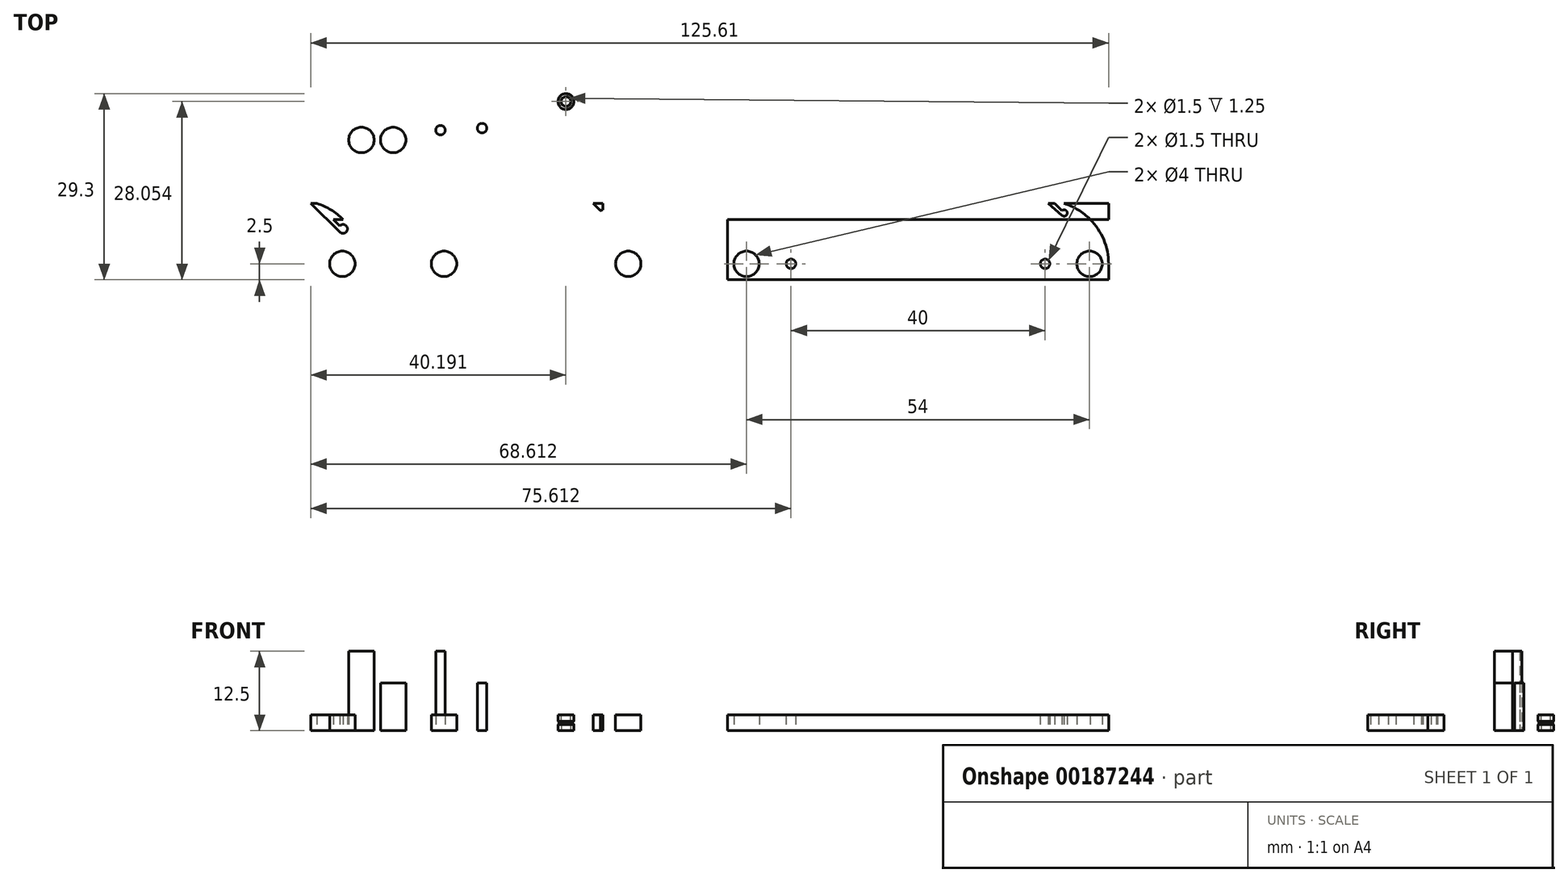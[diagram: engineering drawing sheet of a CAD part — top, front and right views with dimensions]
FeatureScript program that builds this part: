
annotation { "Feature Type Name" : "Feature", "Feature Type Description" : "" }
export const myFeature = defineFeature(function(context is Context, id is Id, definition is map)
    precondition{}
    {
        {
            var Q0;
            Q0=qCreatedBy(makeId("Top.planeOp"),FACE);
            var sketch = newSketch(context, id + "F0", { "sketchPlane" : qUnion([Q0])});
            skLineSegment(sketch, "E0", {"start": v(0, 0) * mm, "end": v(-70, 0) * mm});
            skLineSegment(sketch, "E1", {"start": v(0, 0) * mm, "end": v(70, 0) * mm});
            skLineSegment(sketch, "E2.bottom", {"start": v(-70, 0) * mm, "end": v(-45, 0) * mm});
            skLineSegment(sketch, "E2.top", {"start": v(-70, 12) * mm, "end": v(-53, 12) * mm});
            skLineSegment(sketch, "E2.left", {"start": v(-70, 0) * mm, "end": v(-70, 12) * mm});
            skLineSegment(sketch, "E2.right", {"start": v(-45, 0) * mm, "end": v(-45, 12) * mm});
            skLineSegment(sketch, "E3.bottom", {"start": v(-35, 0) * mm, "end": v(0, 0) * mm});
            skLineSegment(sketch, "E3.top", {"start": v(-35, 12) * mm, "end": v(0, 12) * mm});
            skLineSegment(sketch, "E3.left", {"start": v(-35, 0) * mm, "end": v(-35, 12) * mm});
            skLineSegment(sketch, "E3.right", {"start": v(0, 0) * mm, "end": v(0, 12) * mm});
            skLineSegment(sketch, "E4.bottom", {"start": v(12.61, 0) * mm, "end": v(72.61, 0) * mm});
            skLineSegment(sketch, "E4.top", {"start": v(12.61, 12) * mm, "end": v(63.11, 12) * mm});
            skLineSegment(sketch, "E4.left", {"start": v(12.61, 0) * mm, "end": v(12.61, 12) * mm});
            skLineSegment(sketch, "E4.right", {"start": v(72.61, 0) * mm, "end": v(72.61, 12) * mm});
            skLineSegment(sketch, "E5.bottom", {"start": v(-70, 12) * mm, "end": v(-45, 12) * mm});
            skLineSegment(sketch, "E5.top", {"start": v(-70, 9.5) * mm, "end": v(-45, 9.5) * mm});
            skLineSegment(sketch, "E5.left", {"start": v(-70, 12) * mm, "end": v(-70, 9.5) * mm});
            skLineSegment(sketch, "E5.right", {"start": v(-45, 12) * mm, "end": v(-45, 9.5) * mm});
            skLineSegment(sketch, "E6.bottom", {"start": v(-35, 12) * mm, "end": v(-9.5, 12) * mm});
            skLineSegment(sketch, "E6.top", {"start": v(-35, 9.5) * mm, "end": v(0, 9.5) * mm});
            skLineSegment(sketch, "E6.left", {"start": v(-35, 12) * mm, "end": v(-35, 9.5) * mm});
            skLineSegment(sketch, "E6.right", {"start": v(0, 12) * mm, "end": v(0, 9.5) * mm});
            skLineSegment(sketch, "E7.bottom", {"start": v(12.61, 12) * mm, "end": v(72.61, 12) * mm});
            skLineSegment(sketch, "E7.top", {"start": v(12.61, 9.5) * mm, "end": v(72.61, 9.5) * mm});
            skLineSegment(sketch, "E7.left", {"start": v(12.61, 12) * mm, "end": v(12.61, 9.5) * mm});
            skLineSegment(sketch, "E7.right", {"start": v(72.61, 12) * mm, "end": v(72.61, 9.5) * mm});
            skLineSegment(sketch, "E8", {"start": v(0, 0) * mm, "end": v(0, 2.5) * mm});
            skLineSegment(sketch, "E9", {"start": v(0, 2.5) * mm, "end": v(-3, 2.5) * mm});
            skLineSegment(sketch, "E10", {"start": v(72.61, 0) * mm, "end": v(72.61, 2.5) * mm});
            skLineSegment(sketch, "E11", {"start": v(72.61, 2.5) * mm, "end": v(69.61, 2.5) * mm});
            skLineSegment(sketch, "E12", {"start": v(-45, 0) * mm, "end": v(-45, 2.5) * mm});
            skLineSegment(sketch, "E13", {"start": v(-45, 2.5) * mm, "end": v(-48, 2.5) * mm});
            skCircle(sketch, "E14", {"center": v(-48, 2.5) * mm, "radius": 2 * mm});
            skCircle(sketch, "E15", {"center": v(-3, 2.5) * mm, "radius": 2 * mm});
            skCircle(sketch, "E16", {"center": v(69.61, 2.5) * mm, "radius": 2 * mm});
            skLineSegment(sketch, "E17", {"start": v(0, 12) * mm, "end": v(-7, 12) * mm});
            skLineSegment(sketch, "E18", {"start": v(-45, 12) * mm, "end": v(-52, 12) * mm});
            skLineSegment(sketch, "E19", {"start": v(72.61, 12) * mm, "end": v(65.61, 12) * mm});
            skArc(sketch, "E20", {"start": v(72.61, 2.5) * mm, "mid": v(70.66, 8.4) * mm, "end": v(65.61, 12) * mm});
            skArc(sketch, "E21", {"start": v(0, 2.5) * mm, "mid": v(-1.95, 8.4) * mm, "end": v(-7, 12) * mm});
            skArc(sketch, "E22", {"start": v(-45, 2.5) * mm, "mid": v(-46.95, 8.4) * mm, "end": v(-52, 12) * mm});
            skLineSegment(sketch, "E23", {"start": v(-35, 2.5) * mm, "end": v(-32, 2.5) * mm});
            skCircle(sketch, "E24", {"center": v(-32, 2.5) * mm, "radius": 2 * mm});
            skLineSegment(sketch, "E25", {"start": v(12.61, 2.5) * mm, "end": v(15.61, 2.5) * mm});
            skCircle(sketch, "E26", {"center": v(15.61, 2.5) * mm, "radius": 2 * mm});
            skLineSegment(sketch, "E27.bottom", {"start": v(-70, 22) * mm, "end": v(-66.5, 22) * mm});
            skLineSegment(sketch, "E27.top", {"start": v(-70, 25.5) * mm, "end": v(-66.5, 25.5) * mm});
            skLineSegment(sketch, "E27.left", {"start": v(-70, 22) * mm, "end": v(-70, 25.5) * mm});
            skLineSegment(sketch, "E27.right", {"start": v(-66.5, 22) * mm, "end": v(-66.5, 25.5) * mm});
            skLineSegment(sketch, "E28", {"start": v(-66.5, 25.5) * mm, "end": v(-64.5, 25.5) * mm});
            skLineSegment(sketch, "E29", {"start": v(-64.5, 25.5) * mm, "end": v(-64.5, 23.5) * mm});
            skLineSegment(sketch, "E30", {"start": v(-64.5, 23.5) * mm, "end": v(-66.5, 22) * mm});
            skLineSegment(sketch, "E31", {"start": v(-70, 23.75) * mm, "end": v(-66.5, 23.75) * mm});
            skCircle(sketch, "E32", {"center": v(-68.25, 23.75) * mm, "radius": 1.5 * mm});
            skLineSegment(sketch, "E33", {"start": v(-64.5, 23.5) * mm, "end": v(-65.5, 23.5) * mm});
            skPoint(sketch, "E33.endSnap0", {"position": v(-65.5, 25.5) * mm});
            skLineSegment(sketch, "E34", {"start": v(-65.5, 23.5) * mm, "end": v(-65.5, 24) * mm});
            skCircle(sketch, "E35", {"center": v(-65.5, 24) * mm, "radius": 0.5 * mm});
            skLineSegment(sketch, "E36", {"start": v(-59.5, 25.5) * mm, "end": v(-59.5, 23.5) * mm});
            skLineSegment(sketch, "E37", {"start": v(-59.5, 23.5) * mm, "end": v(-61.5, 22) * mm});
            skLineSegment(sketch, "E38", {"start": v(-61.5, 22) * mm, "end": v(-61.5, 25.5) * mm});
            skLineSegment(sketch, "E39", {"start": v(-61.5, 25.5) * mm, "end": v(-59.5, 25.5) * mm});
            skLineSegment(sketch, "E40", {"start": v(-59.5, 23.5) * mm, "end": v(-60.5, 23.5) * mm});
            skLineSegment(sketch, "E41", {"start": v(-60.5, 23.5) * mm, "end": v(-60.5, 24) * mm});
            skCircle(sketch, "E42", {"center": v(-60.5, 24) * mm, "radius": 0.5 * mm});
            skLineSegment(sketch, "E43", {"start": v(-60.5, 24) * mm, "end": v(-60.5, 24.5) * mm});
            skLineSegment(sketch, "E44", {"start": v(-60.5, 24.5) * mm, "end": v(-61.5, 24.5) * mm});
            skLineSegment(sketch, "E45", {"start": v(-60.5, 23.5) * mm, "end": v(-61.5, 23.5) * mm});
            skLineSegment(sketch, "E46", {"start": v(-61.5, 23.5) * mm, "end": v(-61.5, 23.25) * mm});
            skLineSegment(sketch, "E47", {"start": v(-61.5, 24) * mm, "end": v(-62.15, 24) * mm});
            skCircle(sketch, "E48", {"center": v(-62.15, 24) * mm, "radius": 0.5 * mm});
            skLineSegment(sketch, "E49", {"start": v(-62.15, 24) * mm, "end": v(-62.15, 24.75) * mm});
            skLineSegment(sketch, "E50", {"start": v(-62.15, 24) * mm, "end": v(-62.15, 23.25) * mm});
            skLineSegment(sketch, "E51", {"start": v(-62.15, 24) * mm, "end": v(-62.75, 24) * mm});
            skArc(sketch, "E52", {"start": v(-62.15, 24.75) * mm, "mid": v(-62.75, 24) * mm, "end": v(-62.15, 23.25) * mm});
            skLineSegment(sketch, "E53", {"start": v(-62.15, 24.75) * mm, "end": v(-61.5, 24.75) * mm});
            skLineSegment(sketch, "E54", {"start": v(-62.15, 23.25) * mm, "end": v(-61.5, 23.25) * mm});
            skCircle(sketch, "E55", {"center": v(-45, 22) * mm, "radius": 2 * mm});
            skCircle(sketch, "E56", {"center": v(-40, 22) * mm, "radius": 2 * mm});
            skLineSegment(sketch, "E57", {"start": v(-48.4, 8.49) * mm, "end": v(-52, 12) * mm});
            skLineSegment(sketch, "E58", {"start": v(-53, 12) * mm, "end": v(-48.38, 7.5) * mm});
            skArc(sketch, "E59", {"start": v(-48.38, 7.5) * mm, "mid": v(-47.2, 8) * mm, "end": v(-48.4, 8.49) * mm});
            skPoint(sketch, "E60.orphan", {"position": v(-47.9, 7.03) * mm});
            skLineSegment(sketch, "E61.trimOffspring", {"start": v(-52, 12) * mm, "end": v(-45, 12) * mm});
            skLineSegment(sketch, "E62.bottom", {"start": v(-7, 12) * mm, "end": v(-8.5, 12) * mm});
            skLineSegment(sketch, "E62.left", {"start": v(-7, 12) * mm, "end": v(-7, 10.5) * mm});
            skArc(sketch, "E63", {"start": v(-7.33, 10.12) * mm, "mid": v(-6.5, 10.52) * mm, "end": v(-7.35, 10.85) * mm});
            skLineSegment(sketch, "E64", {"start": v(-7.35, 10.85) * mm, "end": v(-8.5, 12) * mm});
            skLineSegment(sketch, "E65", {"start": v(-8.5, 12) * mm, "end": v(-9.5, 12) * mm});
            skLineSegment(sketch, "E66", {"start": v(-9.5, 12) * mm, "end": v(-7.33, 10.12) * mm});
            skLineSegment(sketch, "E67.trimOffspring", {"start": v(-8.5, 12) * mm, "end": v(0, 12) * mm});
            skArc(sketch, "E68", {"start": v(65.29, 10.12) * mm, "mid": v(66.11, 10.52) * mm, "end": v(65.26, 10.85) * mm});
            skLineSegment(sketch, "E69", {"start": v(65.26, 10.85) * mm, "end": v(64.11, 12) * mm});
            skLineSegment(sketch, "E70", {"start": v(64.11, 12) * mm, "end": v(63.11, 12) * mm});
            skLineSegment(sketch, "E71", {"start": v(63.11, 12) * mm, "end": v(65.29, 10.12) * mm});
            skLineSegment(sketch, "E72.trimOffspring", {"start": v(64.11, 12) * mm, "end": v(72.61, 12) * mm});
            skLineSegment(sketch, "E73", {"start": v(12.61, 0) * mm, "end": v(22.61, 0) * mm});
            skLineSegment(sketch, "E74", {"start": v(22.61, 0) * mm, "end": v(22.61, 2.5) * mm});
            skCircle(sketch, "E75", {"center": v(22.61, 2.5) * mm, "radius": 0.75 * mm});
            skLineSegment(sketch, "E76", {"start": v(72.61, 0) * mm, "end": v(62.61, 0) * mm});
            skLineSegment(sketch, "E77", {"start": v(62.61, 0) * mm, "end": v(62.61, 2.5) * mm});
            skCircle(sketch, "E78", {"center": v(62.61, 2.5) * mm, "radius": 0.75 * mm});
            skLineSegment(sketch, "E79", {"start": v(0, 0) * mm, "end": v(-10, 0) * mm});
            skLineSegment(sketch, "E80", {"start": v(-10, 0) * mm, "end": v(-10, 2.5) * mm});
            skCircle(sketch, "E81", {"center": v(-10, 2.5) * mm, "radius": 0.75 * mm});
            skLineSegment(sketch, "E82", {"start": v(-35, 0) * mm, "end": v(-25, 0) * mm});
            skLineSegment(sketch, "E83", {"start": v(-25, 0) * mm, "end": v(-25, 2.5) * mm});
            skCircle(sketch, "E84", {"center": v(-25, 2.5) * mm, "radius": 0.75 * mm});
            skCircle(sketch, "E85", {"center": v(-47.9, 8) * mm, "radius": 0.7 * mm});
            skSolve(sketch);
        }
        {
            var Q0;
            {var subQ0=sQuery(id+"F0.wireOp",EDGE,"E5.left");Q0=makeQuery(id+"F0.imprint","IMPRINT",FACE,{"disambiguationData":[TD([[makeQuery(id+"F0.imprint","IMPRINT",EDGE,{"derivedFrom":subQ0}),1.0]])]});}
            var Q1;
            Q1=makeQuery(id+"F0.imprint","IMPRINT",FACE,{"disambiguationData":[TD([[makeQuery(id+"F0.imprint","IMPRINT",EDGE,{"derivedFrom":sQuery(id+"F0.wireOp",EDGE,"E7.bottom")}),-1.0]])]});
            var Q2;
            {var subQ0=sQuery(id+"F0.wireOp",EDGE,"E57");var subQ1=sQuery(id+"F0.wireOp",EDGE,"E5.top");var subQ2=makeQuery(id+"F0.imprint","INTERSECT",VERTEX,{"derivedFrom":[subQ1,subQ0]});Q2=makeQuery(id+"F0.imprint","IMPRINT",FACE,{"disambiguationData":[TD([[makeQuery(id+"F0.imprint","IMPRINT",EDGE,{"disambiguationData":[TD([[subQ2,-1.0]])],"derivedFrom":subQ1}),1.0]])]});}
            var Q3;
            Q3=makeQuery(id+"F0.imprint","IMPRINT",FACE,{"disambiguationData":[TD([[makeQuery(id+"F0.imprint","IMPRINT",EDGE,{"derivedFrom":sQuery(id+"F0.wireOp",EDGE,"E6.bottom")}),-1.0]])]});
            var Q4;
            Q4=makeQuery(id+"F0.imprint","IMPRINT",FACE,{"disambiguationData":[TD([[makeQuery(id+"F0.imprint","IMPRINT",EDGE,{"derivedFrom":sQuery(id+"F0.wireOp",EDGE,"E3.bottom")}),1.0]])]});
            var Q5;
            Q5=makeQuery(id+"F0.imprint","IMPRINT",FACE,{"disambiguationData":[TD([[makeQuery(id+"F0.imprint","IMPRINT",EDGE,{"derivedFrom":sQuery(id+"F0.wireOp",EDGE,"E2.bottom")}),1.0]])]});
            var Q6;
            {var subQ8=sQuery(id+"F0.wireOp",EDGE,"E4.bottom");Q6=makeQuery(id+"F0.imprint","IMPRINT",FACE,{"disambiguationData":[TD([[makeQuery(id+"F0.imprint","IMPRINT",EDGE,{"derivedFrom":subQ8}),1.0]])]});}
            var Q7;
            Q7=makeQuery(id+"F0.imprint","IMPRINT",FACE,{"disambiguationData":[TD([[makeQuery(id+"F0.imprint","IMPRINT",EDGE,{"derivedFrom":sQuery(id+"F0.wireOp",EDGE,"E14")}),1.0]])]});
            var Q8;
            Q8=makeQuery(id+"F0.imprint","IMPRINT",FACE,{"disambiguationData":[TD([[makeQuery(id+"F0.imprint","IMPRINT",EDGE,{"derivedFrom":sQuery(id+"F0.wireOp",EDGE,"E15")}),1.0]])]});
            var Q9;
            Q9=makeQuery(id+"F0.imprint","IMPRINT",FACE,{"disambiguationData":[TD([[makeQuery(id+"F0.imprint","IMPRINT",EDGE,{"derivedFrom":sQuery(id+"F0.wireOp",EDGE,"E24")}),1.0]])]});
            var Q10;
            Q10=makeQuery(id+"F0.imprint","IMPRINT",FACE,{"disambiguationData":[TD([[makeQuery(id+"F0.imprint","IMPRINT",EDGE,{"derivedFrom":sQuery(id+"F0.wireOp",EDGE,"E16")}),1.0]])]});
            var Q11;
            Q11=makeQuery(id+"F0.imprint","IMPRINT",FACE,{"disambiguationData":[TD([[makeQuery(id+"F0.imprint","IMPRINT",EDGE,{"derivedFrom":sQuery(id+"F0.wireOp",EDGE,"E26")}),1.0]])]});
            var Q12;
            {var subQ3=sQuery(id+"F0.wireOp",EDGE,"E58");var subQ5=sQuery(id+"F0.wireOp",EDGE,"E5.top");var subQ6=makeQuery(id+"F0.imprint","INTERSECT",VERTEX,{"derivedFrom":[subQ5,subQ3]});Q12=makeQuery(id+"F0.imprint","IMPRINT",FACE,{"disambiguationData":[TD([[makeQuery(id+"F0.imprint","IMPRINT",EDGE,{"disambiguationData":[TD([[subQ6,-1.0]])],"derivedFrom":subQ5}),1.0]])]});}
            var Q13;
            {var subQ5=sQuery(id+"F0.wireOp",EDGE,"E59");Q13=makeQuery(id+"F0.imprint","IMPRINT",FACE,{"disambiguationData":[TD([[makeQuery(id+"F0.imprint","IMPRINT",EDGE,{"derivedFrom":subQ5}),1.0]])]});}
            var Q14;
            {var subQ0=sQuery(id+"F0.wireOp",EDGE,"E58");var subQ1=sQuery(id+"F0.wireOp",EDGE,"E5.top");var subQ2=makeQuery(id+"F0.imprint","INTERSECT",VERTEX,{"derivedFrom":[subQ1,subQ0]});Q14=makeQuery(id+"F0.imprint","IMPRINT",FACE,{"disambiguationData":[TD([[makeQuery(id+"F0.imprint","IMPRINT",EDGE,{"disambiguationData":[TD([[subQ2,-1.0]])],"derivedFrom":subQ1}),-1.0]])]});}
            var Q15;
            {var subQ5=sQuery(id+"F0.wireOp",EDGE,"E64");Q15=makeQuery(id+"F0.imprint","IMPRINT",FACE,{"disambiguationData":[TD([[makeQuery(id+"F0.imprint","IMPRINT",EDGE,{"derivedFrom":subQ5}),-1.0]])]});}
            extrude(context, id + "F1", {"entities" : qUnion([Q0, Q1, Q2, Q3, Q4, Q5, Q6, Q7, Q8, Q9, Q10, Q11, Q12, Q13, Q14, Q15]), "depth" : 2.5 * mm});
        }
        {
            var Q0;
            Q0=sQuery(id+"F0.wireOp",VERTEX,"E9.end");
            var Q1;
            Q1=sQuery(id+"F0.wireOp",VERTEX,"E16.center");
            var Q2;
            Q2=sQuery(id+"F0.wireOp",VERTEX,"E13.end");
            var Q3;
            Q3=sQuery(id+"F0.wireOp",VERTEX,"E23.end");
            var Q4;
            Q4=sQuery(id+"F0.wireOp",VERTEX,"E25.end");
            var Q5;
            Q5=makeQuery(id+"F1.opExtrude","SWEPT_BODY",BODY,{"disambiguationData":[OSD([sQuery(id+"F0.wireOp",EDGE,"E2.bottom"),sQuery(id+"F0.wireOp",EDGE,"E2.left"),sQuery(id+"F0.wireOp",EDGE,"E5.bottom"),sQuery(id+"F0.wireOp",EDGE,"E5.left"),sQuery(id+"F0.wireOp",EDGE,"E12"),sQuery(id+"F0.wireOp",EDGE,"E22")])]});
            var Q6;
            Q6=makeQuery(id+"F1.opExtrude","SWEPT_BODY",BODY,{"disambiguationData":[OSD([sQuery(id+"F0.wireOp",EDGE,"E3.bottom"),sQuery(id+"F0.wireOp",EDGE,"E3.left"),sQuery(id+"F0.wireOp",EDGE,"E6.bottom"),sQuery(id+"F0.wireOp",EDGE,"E6.left"),sQuery(id+"F0.wireOp",EDGE,"E8"),sQuery(id+"F0.wireOp",EDGE,"E21")])]});
            var Q7;
            Q7=makeQuery(id+"F1.opExtrude","SWEPT_BODY",BODY,{"disambiguationData":[OSD([sQuery(id+"F0.wireOp",EDGE,"E4.bottom"),sQuery(id+"F0.wireOp",EDGE,"E4.left"),sQuery(id+"F0.wireOp",EDGE,"E7.bottom"),sQuery(id+"F0.wireOp",EDGE,"E7.left"),sQuery(id+"F0.wireOp",EDGE,"E10"),sQuery(id+"F0.wireOp",EDGE,"E20")])]});
            hole(context, id + "F2", {"style" : HoleStyle.SIMPLE, "endStyle" : HoleEndStyle.BLIND, "oppositeDirection" : true, "holeDiameter" : 4 * mm, "holeDepth" : 16 * mm, "locations" : qUnion([Q0, Q1, Q2, Q3, Q4]), "scope" : qUnion([Q5, Q6, Q7])});
        }
        {
            var Q0;
            Q0=makeQuery(id+"F0.imprint","IMPRINT",FACE,{"disambiguationData":[TD([[makeQuery(id+"F0.imprint","IMPRINT",EDGE,{"derivedFrom":sQuery(id+"F0.wireOp",EDGE,"E55")}),1.0]])]});
            extrude(context, id + "F3", {"entities" : qUnion([Q0]), "depth" : 12.5 * mm});
        }
        {
            var Q0;
            Q0=qCreatedBy(makeId("Top.planeOp"),FACE);
            var sketch = newSketch(context, id + "F4", { "sketchPlane" : qUnion([Q0])});
            skCircle(sketch, "E86", {"center": v(-32.56, 23.55) * mm, "radius": 0.75 * mm});
            skCircle(sketch, "E87", {"center": v(-26.02, 23.87) * mm, "radius": 0.75 * mm});
            skSolve(sketch);
        }
        {
            var Q0;
            Q0=makeQuery(id+"F4.imprint","IMPRINT",FACE,{"disambiguationData":[TD([[makeQuery(id+"F4.imprint","IMPRINT",EDGE,{"derivedFrom":sQuery(id+"F4.wireOp",EDGE,"E86")}),1.0]])]});
            extrude(context, id + "F5", {"entities" : qUnion([Q0]), "depth" : 12.5 * mm});
        }
        {
            var Q0;
            Q0=makeQuery(id+"F4.imprint","IMPRINT",FACE,{"disambiguationData":[TD([[makeQuery(id+"F4.imprint","IMPRINT",EDGE,{"derivedFrom":sQuery(id+"F4.wireOp",EDGE,"E87")}),1.0]])]});
            var Q1;
            Q1=sQuery(id+"F4.wireOp",EDGE,"E87");
            extrude(context, id + "F6", {"entities" : qUnion([Q0]), "surfaceEntities" : qUnion([Q1]), "depth" : 7.5 * mm});
        }
        {
            var Q0;
            Q0=makeQuery(id+"F0.imprint","IMPRINT",FACE,{"disambiguationData":[TD([[makeQuery(id+"F0.imprint","IMPRINT",EDGE,{"derivedFrom":sQuery(id+"F0.wireOp",EDGE,"E56")}),1.0]])]});
            extrude(context, id + "F7", {"entities" : qUnion([Q0]), "depth" : 7.5 * mm});
        }
        {
            var Q0;
            Q0=qCreatedBy(makeId("Top.planeOp"),FACE);
            var sketch = newSketch(context, id + "F8", { "sketchPlane" : qUnion([Q0])});
            skCircle(sketch, "E88", {"center": v(-12.8, 28.05) * mm, "radius": 1.25 * mm});
            skCircle(sketch, "E89", {"center": v(-12.8, 28.05) * mm, "radius": 0.75 * mm});
            skSolve(sketch);
        }
        {
            var Q0;
            Q0 = qSketchRegion(id + "F8", true);
            extrude(context, id + "F9", {"entities" : qUnion([Q0]), "depth" : (2.5 / 2) * mm});
        }
        {
            var Q0;
            Q0=makeQuery(id+"F9.opExtrude","CAP_EDGE",EDGE,{"disambiguationData":[OSD([sQuery(id+"F8.wireOp",EDGE,"E88")])],"isStart":false});
            chamfer(context, id + "F10", {"entities" : qUnion([Q0]), "width" : 0.25 * mm, "tangentPropagation" : true});
        }
        {
            var Q0;
            Q0=makeQuery(id+"F9.opExtrude","SWEPT_BODY",BODY,{"disambiguationData":[OSD([sQuery(id+"F8.wireOp",EDGE,"E88"),sQuery(id+"F8.wireOp",EDGE,"E89")])]});
            var Q1;
            Q1=makeQuery(id+"F9.opExtrude","CAP_FACE",FACE,{"disambiguationData":[OSD([sQuery(id+"F8.wireOp",EDGE,"E88"),sQuery(id+"F8.wireOp",EDGE,"E89")])],"isStart":false});
            mirror(context, id + "F11", {"operationType" : NewBodyOperationType.ADD, "entities" : qUnion([Q0]), "mirrorPlane" : qUnion([Q1])});
        }
    });
